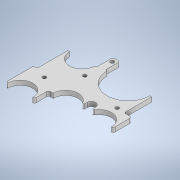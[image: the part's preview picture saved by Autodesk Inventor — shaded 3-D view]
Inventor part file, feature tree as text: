
AUTODESK INVENTOR PART (.ipt)
format: ipt  version: 2021 (Build 250183000, 183)  size: 283,648 bytes
history: native  units: mm
features: sketch x4, extrude x3, hole x2, fillet x1
ambient origin geometry x8: Origin, YZ Plane, XZ Plane, XY Plane, X Axis, Y Axis, Z Axis, Center Point
bodies: Solid1 (feature_tree)
feature tree (10):
  extrude  "Extrusion1"  Depth=116.5mm
  extrude  "Extrusion2"  Depth=5.0mm
  extrude  "Extrusion3"  Depth=27.7mm
  fillet  "Fillet2"  Radius=27.7mm
  sketch  "Sketch7"  dims[d8=27.7mm d9=116.5mm d10=112.5mm d13=37.0mm d14=18.5mm d15=30.9mm d16=5.0mm d17=0.0mm d18=19.5mm d19=35.0mm d20=35.0mm d26=2.0mm d27=2.0mm d28=2.0mm d29=2.0mm d30=2.0mm d32=2.0mm d33=2.0mm d34=2.0mm d35=2.0mm d36=10.0mm d37=0.0mm d38=27.7mm d39=10.0mm d40=10.0mm d42=25.8mm d43=28.0mm d45=25.8mm d46=23.25mm d47=23.25mm d50=37.0mm d53=27.7mm d54=27.7mm d56=19.15mm d57=50.85mm d58=46.75mm d59=2.0mm d60=6.182153mm d61=31.7mm d63=30.9mm d64=3.4mm d65=11.9mm d66=61.0mm d67=47.7mm d68=28.0mm d69=18.5mm d71=30.27mm d72=27.7mm d73=2.0mm d74=30.27mm d75=2.0mm d76=112.5mm d77=116.5mm d78=1.0mm d79=14.0mm d80=2.0mm d81=51.7mm d82=2.0mm d83=13.0mm d84=34.0mm d85=36.0mm d86=2.0mm d87=11.0mm d88=13.0mm d89=3.8mm d90=6.0mm d91=4.0mm d92=2.0mm d93=90.0deg d94=8.0mm d95=20.594885mm d96=3.85mm d97=4.5mm d98=4.2mm d99=6.0mm d100=4.0mm d101=2.0mm d102=90.0deg d103=8.0mm d104=20.594885mm]
  hole  "Hole1"  [1 undecoded]
  hole  "Hole2"  [1 undecoded]
  sketch  "Sketch1"  dims[d0=112.5mm d1=116.5mm]
  sketch  "Sketch2"  dims[d2=5.0mm d3=0.0mm d4=47.7mm]
  sketch  "Sketch5"  dims[d5=27.7mm d6=27.7mm d7=27.7mm]
note: 2 required parameter values undecoded (feature->parameter linkage not recoverable at this tier; creation-order binding heuristic only, values carry confidence <= 0.55)
